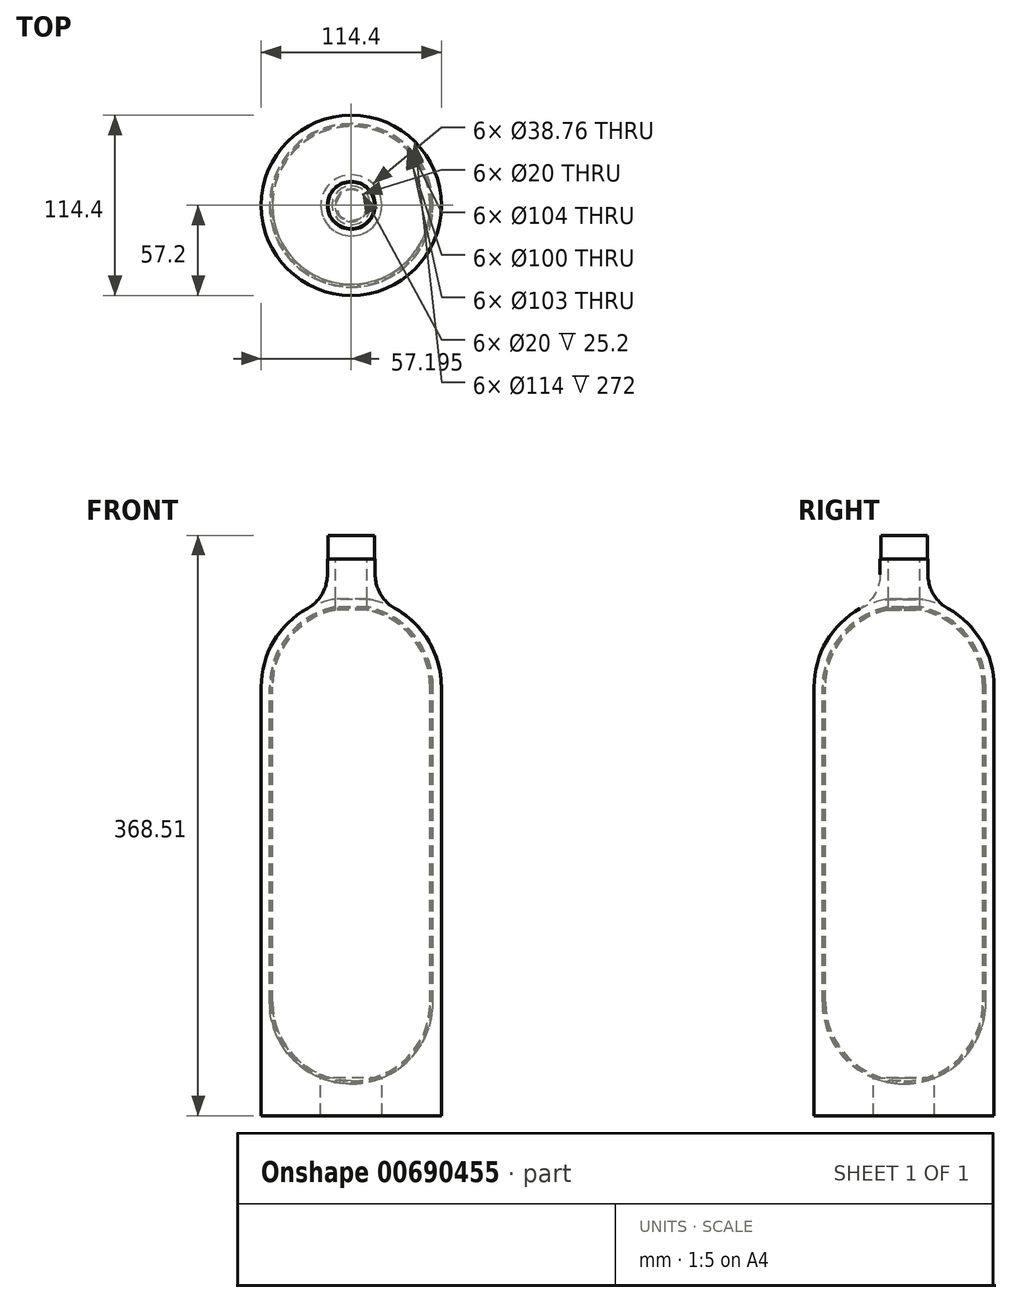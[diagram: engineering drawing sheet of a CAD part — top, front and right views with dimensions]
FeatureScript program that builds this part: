
annotation { "Feature Type Name" : "Feature", "Feature Type Description" : "" }
export const myFeature = defineFeature(function(context is Context, id is Id, definition is map)
    precondition{}
    {
        {
            var Q0;
            Q0=qCreatedBy(makeId("Front.planeOp"),FACE);
            var sketch = newSketch(context, id + "F0", { "sketchPlane" : qUnion([Q0])});
            skLineSegment(sketch, "E0.left", {"start": v(-41.55, 81.82) * mm, "end": v(-41.55, -118.18) * mm});
            skLineSegment(sketch, "E0.right", {"start": v(58.45, 81.82) * mm, "end": v(58.45, -118.18) * mm});
            skArc(sketch, "E1", {"start": v(58.45, 81.82) * mm, "mid": v(47.43, 113.13) * mm, "end": v(19.23, 130.64) * mm});
            skArc(sketch, "E2", {"start": v(-41.55, -118.18) * mm, "mid": v(8.45, -168.18) * mm, "end": v(58.45, -118.18) * mm});
            skPoint(sketch, "E3", {"position": v(8.45, 131.82) * mm});
            skPoint(sketch, "E4", {"position": v(8.45, -168.18) * mm});
            skLineSegment(sketch, "E5", {"start": v(8.45, 268.9) * mm, "end": v(8.45, 161.4) * mm, "construction": true});
            skArc(sketch, "E6.0", {"start": v(60.45, 81.82) * mm, "mid": v(48.99, 114.38) * mm, "end": v(19.66, 132.6) * mm});
            skLineSegment(sketch, "E6.1", {"start": v(60.45, 81.82) * mm, "end": v(60.45, -118.18) * mm});
            skArc(sketch, "E6.2", {"start": v(-43.55, -118.18) * mm, "mid": v(8.45, -170.18) * mm, "end": v(60.45, -118.18) * mm});
            skLineSegment(sketch, "E6.3", {"start": v(-43.55, 81.82) * mm, "end": v(-43.55, -118.18) * mm});
            skLineSegment(sketch, "E7", {"start": v(18.45, 131.62) * mm, "end": v(18.45, 131.62) * mm});
            skLineSegment(sketch, "E8.left", {"start": v(8.45, 161.4) * mm, "end": v(8.45, 131.4) * mm, "construction": true});
            skLineSegment(sketch, "E9", {"start": v(-1.55, 131.62) * mm, "end": v(-1.55, 131.62) * mm});
            skPoint(sketch, "E10.orphan", {"position": v(-1.55, 147.69) * mm});
            skArc(sketch, "E11.trimOffspring", {"start": v(-2.77, 132.6) * mm, "mid": v(-32.1, 114.38) * mm, "end": v(-43.55, 81.82) * mm});
            skArc(sketch, "E12.trimOffspring", {"start": v(-2.34, 130.64) * mm, "mid": v(-30.54, 113.13) * mm, "end": v(-41.55, 81.82) * mm});
            skPoint(sketch, "E13.end.orphan", {"position": v(-1.55, 117.69) * mm});
            skPoint(sketch, "E14.start.orphan", {"position": v(8.45, 117.69) * mm});
            skLineSegment(sketch, "E15.trimOffspring", {"start": v(8.45, 131.4) * mm, "end": v(8.45, -295.6) * mm, "construction": true});
            skPoint(sketch, "E16.visualSharp", {"position": v(18.45, 130.8) * mm});
            skArc(sketch, "E16.filletArc", {"start": v(18.45, 131.62) * mm, "mid": v(18.67, 130.99) * mm, "end": v(19.23, 130.64) * mm});
            skPoint(sketch, "E17.visualSharp", {"position": v(18.45, 132.85) * mm});
            skArc(sketch, "E17.filletArc", {"start": v(19.66, 132.6) * mm, "mid": v(18.82, 132.4) * mm, "end": v(18.45, 131.62) * mm});
            skPoint(sketch, "E18.visualSharp", {"position": v(-1.55, 130.8) * mm});
            skArc(sketch, "E18.filletArc", {"start": v(-2.34, 130.64) * mm, "mid": v(-1.78, 130.99) * mm, "end": v(-1.55, 131.62) * mm});
            skPoint(sketch, "E19.newPointB", {"position": v(-1.55, 132.69) * mm});
            skArc(sketch, "E19.filletArc", {"start": v(-1.55, 131.62) * mm, "mid": v(-1.93, 132.4) * mm, "end": v(-2.77, 132.6) * mm});
            skArc(sketch, "E20.0", {"start": v(65.45, 81.82) * mm, "mid": v(57.53, 110.8) * mm, "end": v(35.97, 131.73) * mm});
            skArc(sketch, "E20.1", {"start": v(-19.36, 131.57) * mm, "mid": v(-40.72, 110.66) * mm, "end": v(-48.55, 81.82) * mm});
            skLineSegment(sketch, "E20.2", {"start": v(-48.55, 81.82) * mm, "end": v(-48.55, -118.18) * mm});
            skLineSegment(sketch, "E20.4", {"start": v(65.45, 81.82) * mm, "end": v(65.45, -118.18) * mm});
            skLineSegment(sketch, "E21", {"start": v(-1.55, 131.62) * mm, "end": v(-1.55, 137.93) * mm});
            skLineSegment(sketch, "E22", {"start": v(18.45, 131.62) * mm, "end": v(18.45, 137.93) * mm});
            skArc(sketch, "E23.trimOffspring", {"start": v(65.45, 81.82) * mm, "mid": v(52.88, 117.51) * mm, "end": v(20.74, 137.47) * mm});
            skArc(sketch, "E24.trimOffspring", {"start": v(-3.85, 137.47) * mm, "mid": v(-36, 117.51) * mm, "end": v(-48.55, 81.82) * mm});
            skLineSegment(sketch, "E25", {"start": v(-3.85, 137.47) * mm, "end": v(-1.55, 137.93) * mm});
            skLineSegment(sketch, "E26", {"start": v(20.74, 137.47) * mm, "end": v(18.45, 137.93) * mm});
            skPoint(sketch, "E27", {"position": v(8.45, -170.18) * mm});
            skLineSegment(sketch, "E28", {"start": v(8.45, -170.18) * mm, "end": v(8.45, -190.18) * mm});
            skLineSegment(sketch, "E29", {"start": v(8.45, -190.18) * mm, "end": v(27.82, -190.18) * mm});
            skLineSegment(sketch, "E30", {"start": v(27.82, -190.18) * mm, "end": v(27.82, -166.44) * mm});
            skLineSegment(sketch, "E31", {"start": v(8.45, -190.18) * mm, "end": v(-11.55, -190.18) * mm});
            skLineSegment(sketch, "E32", {"start": v(-11.55, -190.18) * mm, "end": v(-11.55, -166.18) * mm});
            skLineSegment(sketch, "E33", {"start": v(-48.55, -118.18) * mm, "end": v(-48.55, -190.18) * mm});
            skLineSegment(sketch, "E34", {"start": v(-48.55, -190.18) * mm, "end": v(-11.55, -190.18) * mm});
            skLineSegment(sketch, "E35", {"start": v(65.45, -118.18) * mm, "end": v(65.45, -190.18) * mm});
            skLineSegment(sketch, "E36", {"start": v(65.45, -190.18) * mm, "end": v(27.82, -190.18) * mm});
            skLineSegment(sketch, "E37", {"start": v(-1.55, 137.93) * mm, "end": v(-1.55, 162.93) * mm});
            skLineSegment(sketch, "E38", {"start": v(18.45, 137.93) * mm, "end": v(18.45, 162.93) * mm});
            skLineSegment(sketch, "E39", {"start": v(18.65, 162.93) * mm, "end": v(23.05, 162.93) * mm});
            skLineSegment(sketch, "E40", {"start": v(23.05, 162.93) * mm, "end": v(23.05, 153.62) * mm});
            skLineSegment(sketch, "E41", {"start": v(-1.75, 162.93) * mm, "end": v(-6.55, 162.93) * mm});
            skLineSegment(sketch, "E42", {"start": v(-6.55, 162.93) * mm, "end": v(-6.55, 153.4) * mm});
            skArc(sketch, "E43.filletArc", {"start": v(-19.36, 131.57) * mm, "mid": v(-10, 140.75) * mm, "end": v(-6.55, 153.4) * mm});
            skArc(sketch, "E44.filletArc", {"start": v(23.05, 153.62) * mm, "mid": v(26.52, 140.9) * mm, "end": v(35.97, 131.73) * mm});
            skLineSegment(sketch, "E45.1", {"start": v(-1.55, 163.13) * mm, "end": v(-6.75, 163.13) * mm});
            skLineSegment(sketch, "E45.2", {"start": v(-6.75, 163.13) * mm, "end": v(-6.75, 153.4) * mm});
            skArc(sketch, "E45.3", {"start": v(-19.46, 131.75) * mm, "mid": v(-10.16, 140.85) * mm, "end": v(-6.75, 153.4) * mm});
            skArc(sketch, "E45.4", {"start": v(-19.46, 131.75) * mm, "mid": v(-40.89, 110.76) * mm, "end": v(-48.75, 81.82) * mm});
            skLineSegment(sketch, "E45.5", {"start": v(-48.75, 81.82) * mm, "end": v(-48.75, -118.18) * mm});
            skLineSegment(sketch, "E45.6", {"start": v(-48.75, -118.18) * mm, "end": v(-48.75, -190.38) * mm});
            skLineSegment(sketch, "E45.7", {"start": v(-48.75, -190.38) * mm, "end": v(-11.55, -190.38) * mm});
            skArc(sketch, "E45.8", {"start": v(23.25, 153.62) * mm, "mid": v(26.7, 141.01) * mm, "end": v(36.07, 131.9) * mm});
            skLineSegment(sketch, "E45.9", {"start": v(23.25, 163.13) * mm, "end": v(23.25, 153.62) * mm});
            skLineSegment(sketch, "E45.10", {"start": v(18.45, 163.13) * mm, "end": v(23.25, 163.13) * mm});
            skArc(sketch, "E45.12", {"start": v(65.65, 81.82) * mm, "mid": v(57.7, 110.9) * mm, "end": v(36.07, 131.9) * mm});
            skLineSegment(sketch, "E45.13", {"start": v(65.65, 81.82) * mm, "end": v(65.65, -118.18) * mm});
            skLineSegment(sketch, "E45.14", {"start": v(65.65, -118.18) * mm, "end": v(65.65, -190.38) * mm});
            skLineSegment(sketch, "E45.15", {"start": v(65.65, -190.38) * mm, "end": v(27.82, -190.38) * mm});
            skLineSegment(sketch, "E45.16", {"start": v(8.45, -190.38) * mm, "end": v(27.82, -190.38) * mm});
            skLineSegment(sketch, "E45.17", {"start": v(8.45, -190.38) * mm, "end": v(-11.55, -190.38) * mm});
            skLineSegment(sketch, "E46", {"start": v(8.45, -190.18) * mm, "end": v(8.45, -190.38) * mm});
            skLineSegment(sketch, "E47", {"start": v(8.45, -168.18) * mm, "end": v(8.45, -170.18) * mm});
            skLineSegment(sketch, "E48.0", {"start": v(58.95, 81.82) * mm, "end": v(58.95, -118.18) * mm});
            skArc(sketch, "E48.1", {"start": v(-42.05, -118.18) * mm, "mid": v(8.45, -168.68) * mm, "end": v(58.95, -118.18) * mm});
            skLineSegment(sketch, "E48.2", {"start": v(-42.05, 81.82) * mm, "end": v(-42.05, -118.18) * mm});
            skLineSegment(sketch, "E48.3", {"start": v(59.95, 81.82) * mm, "end": v(59.95, -118.18) * mm});
            skArc(sketch, "E48.4", {"start": v(59.95, 81.82) * mm, "mid": v(48.6, 114.07) * mm, "end": v(19.55, 132.1) * mm});
            skArc(sketch, "E48.5", {"start": v(19.55, 132.1) * mm, "mid": v(19.13, 132) * mm, "end": v(18.95, 131.62) * mm});
            skArc(sketch, "E48.6", {"start": v(18.95, 131.62) * mm, "mid": v(19.06, 131.3) * mm, "end": v(19.34, 131.13) * mm});
            skArc(sketch, "E48.7", {"start": v(-43.05, -118.18) * mm, "mid": v(8.45, -169.68) * mm, "end": v(59.95, -118.18) * mm});
            skLineSegment(sketch, "E48.8", {"start": v(-43.05, 81.82) * mm, "end": v(-43.05, -118.18) * mm});
            skArc(sketch, "E48.9", {"start": v(-2.66, 132.1) * mm, "mid": v(-31.7, 114.07) * mm, "end": v(-43.05, 81.82) * mm});
            skArc(sketch, "E48.10", {"start": v(58.95, 81.82) * mm, "mid": v(47.82, 113.44) * mm, "end": v(19.34, 131.13) * mm});
            skArc(sketch, "E48.11", {"start": v(-2.05, 131.62) * mm, "mid": v(-2.24, 132) * mm, "end": v(-2.66, 132.1) * mm});
            skArc(sketch, "E48.12", {"start": v(-2.45, 131.13) * mm, "mid": v(-2.16, 131.3) * mm, "end": v(-2.05, 131.62) * mm});
            skArc(sketch, "E48.13", {"start": v(-2.45, 131.13) * mm, "mid": v(-30.93, 113.44) * mm, "end": v(-42.05, 81.82) * mm});
            skLineSegment(sketch, "E49", {"start": v(-1.55, 131.62) * mm, "end": v(-1.55, 130.8) * mm});
            skLineSegment(sketch, "E50", {"start": v(-1.55, 131.62) * mm, "end": v(18.45, 131.62) * mm});
            skLineSegment(sketch, "E51", {"start": v(18.45, 131.62) * mm, "end": v(18.45, 130.8) * mm});
            skLineSegment(sketch, "E52", {"start": v(-1.55, 130.8) * mm, "end": v(18.45, 130.8) * mm});
            skLineSegment(sketch, "E53", {"start": v(18.65, 137.93) * mm, "end": v(18.65, 162.93) * mm});
            skLineSegment(sketch, "E54", {"start": v(18.45, 162.93) * mm, "end": v(18.45, 163.13) * mm});
            skLineSegment(sketch, "E55", {"start": v(18.65, 137.93) * mm, "end": v(18.65, 137.9) * mm});
            skLineSegment(sketch, "E56", {"start": v(-1.75, 137.93) * mm, "end": v(-1.75, 137.9) * mm});
            skLineSegment(sketch, "E57", {"start": v(-1.75, 137.93) * mm, "end": v(-1.75, 162.93) * mm});
            skLineSegment(sketch, "E58", {"start": v(-1.55, 162.93) * mm, "end": v(-1.55, 163.13) * mm});
            skLineSegment(sketch, "E59.bottom", {"start": v(-6.75, 163.13) * mm, "end": v(23.25, 163.13) * mm});
            skLineSegment(sketch, "E59.top", {"start": v(-6.75, 178.13) * mm, "end": v(23.25, 178.13) * mm});
            skLineSegment(sketch, "E59.left", {"start": v(-6.75, 163.13) * mm, "end": v(-6.75, 178.13) * mm});
            skLineSegment(sketch, "E59.right", {"start": v(23.25, 163.13) * mm, "end": v(23.25, 178.13) * mm});
            skLineSegment(sketch, "E60.top", {"start": v(-1.55, 163.13) * mm, "end": v(18.45, 163.13) * mm});
            skLineSegment(sketch, "E60.left", {"start": v(-1.55, 131.62) * mm, "end": v(-1.55, 163.13) * mm});
            skLineSegment(sketch, "E60.right", {"start": v(18.45, 131.62) * mm, "end": v(18.45, 163.13) * mm});
            skLineSegment(sketch, "E61", {"start": v(8.45, 178.13) * mm, "end": v(8.45, 130.8) * mm});
            skLineSegment(sketch, "E62", {"start": v(8.45, 130.8) * mm, "end": v(8.45, 131.62) * mm});
            skPoint(sketch, "E63", {"position": v(8.45, 163.13) * mm});
            skLineSegment(sketch, "E64", {"start": v(-1.55, 137.93) * mm, "end": v(18.45, 137.93) * mm});
            skSolve(sketch);
        }
        {
            var Q0;
            {var subQ0=sQuery(id+"F0.wireOp",EDGE,"E28");Q0=makeQuery(id+"F0.imprint","IMPRINT",FACE,{"disambiguationData":[TD([[makeQuery(id+"F0.imprint","IMPRINT",EDGE,{"derivedFrom":subQ0}),1.0]])]});}
            var Q1;
            Q1=sQuery(id+"F0.wireOp",EDGE,"E15.trimOffspring");
            revolve(context, id + "F1", {"entities" : qUnion([Q0]), "axis" : qUnion([Q1]), "revolveType" : RevolveType.FULL});
        }
        {
            var Q0;
            {var subQ1=sQuery(id+"F0.wireOp",EDGE,"E20.2");Q0=makeQuery(id+"F0.imprint","IMPRINT",FACE,{"disambiguationData":[TD([[makeQuery(id+"F0.imprint","IMPRINT",EDGE,{"derivedFrom":subQ1}),-1.0]])]});}
            var Q1;
            Q1=makeQuery(id+"F0.imprint","IMPRINT",FACE,{"disambiguationData":[TD([[makeQuery(id+"F0.imprint","IMPRINT",EDGE,{"derivedFrom":sQuery(id+"F0.wireOp",EDGE,"E42")}),1.0]])]});
            var Q2;
            Q2=sQuery(id+"F0.wireOp",EDGE,"E15.trimOffspring");
            revolve(context, id + "F2", {"entities" : qUnion([Q0, Q1]), "axis" : qUnion([Q2]), "revolveType" : RevolveType.FULL});
        }
        {
            var Q0;
            Q0=makeQuery(id+"F0.imprint","IMPRINT",FACE,{"disambiguationData":[TD([[makeQuery(id+"F0.imprint","IMPRINT",EDGE,{"derivedFrom":sQuery(id+"F0.wireOp",EDGE,"E6.0")}),-1.0]])]});
            var Q1;
            Q1=sQuery(id+"F0.wireOp",EDGE,"E15.trimOffspring");
            revolve(context, id + "F3", {"entities" : qUnion([Q0]), "axis" : qUnion([Q1]), "revolveType" : RevolveType.FULL});
        }
        {
            var Q0;
            {var subQ12=sQuery(id+"F0.wireOp",EDGE,"E0.right");Q0=makeQuery(id+"F0.imprint","IMPRINT",FACE,{"disambiguationData":[TD([[makeQuery(id+"F0.imprint","IMPRINT",EDGE,{"derivedFrom":subQ12}),1.0]])]});}
            var Q1;
            Q1=sQuery(id+"F0.wireOp",EDGE,"E15.trimOffspring");
            revolve(context, id + "F4", {"entities" : qUnion([Q0]), "axis" : qUnion([Q1]), "revolveType" : RevolveType.FULL});
        }
        {
            var Q0;
            {var subQ1=sQuery(id+"F0.wireOp",EDGE,"E60.top");var subQ3=sQuery(id+"F0.wireOp",EDGE,"E61");var subQ4=makeQuery(id+"F0.imprint","INTERSECT",VERTEX,{"derivedFrom":[subQ1,subQ3]});Q0=makeQuery(id+"F0.imprint","IMPRINT",FACE,{"disambiguationData":[TD([[makeQuery(id+"F0.imprint","IMPRINT",EDGE,{"disambiguationData":[TD([[subQ4,-1.0]])],"derivedFrom":subQ3}),1.0]])]});}
            var Q1;
            {var subQ5=sQuery(id+"F0.wireOp",EDGE,"E59.right");Q1=makeQuery(id+"F0.imprint","IMPRINT",FACE,{"disambiguationData":[TD([[makeQuery(id+"F0.imprint","IMPRINT",EDGE,{"derivedFrom":subQ5}),1.0]])]});}
            var Q2;
            Q2=sQuery(id+"F0.wireOp",EDGE,"E15.trimOffspring");
            revolve(context, id + "F5", {"entities" : qUnion([Q0, Q1]), "axis" : qUnion([Q2]), "revolveType" : RevolveType.FULL});
        }
        {
            var Q0;
            {var subQ3=sQuery(id+"F0.wireOp",EDGE,"E61");var subQ5=sQuery(id+"F0.wireOp",EDGE,"E64");var subQ7=makeQuery(id+"F0.imprint","INTERSECT",VERTEX,{"derivedFrom":[subQ3,subQ5]});Q0=makeQuery(id+"F0.imprint","IMPRINT",FACE,{"disambiguationData":[TD([[makeQuery(id+"F0.imprint","IMPRINT",EDGE,{"disambiguationData":[TD([[subQ7,-1.0]])],"derivedFrom":subQ3}),1.0]])]});}
            var Q1;
            Q1=sQuery(id+"F0.wireOp",EDGE,"E15.trimOffspring");
            revolve(context, id + "F6", {"entities" : qUnion([Q0]), "axis" : qUnion([Q1]), "revolveType" : RevolveType.FULL});
        }
        {
            var Q0;
            {var subQ0=sQuery(id+"F0.wireOp",EDGE,"E51");Q0=makeQuery(id+"F0.imprint","IMPRINT",FACE,{"disambiguationData":[TD([[makeQuery(id+"F0.imprint","IMPRINT",EDGE,{"derivedFrom":subQ0}),-1.0]])]});}
            var Q1;
            Q1=sQuery(id+"F0.wireOp",EDGE,"E15.trimOffspring");
            revolve(context, id + "F7", {"entities" : qUnion([Q0]), "axis" : qUnion([Q1]), "revolveType" : RevolveType.FULL});
        }
    });
